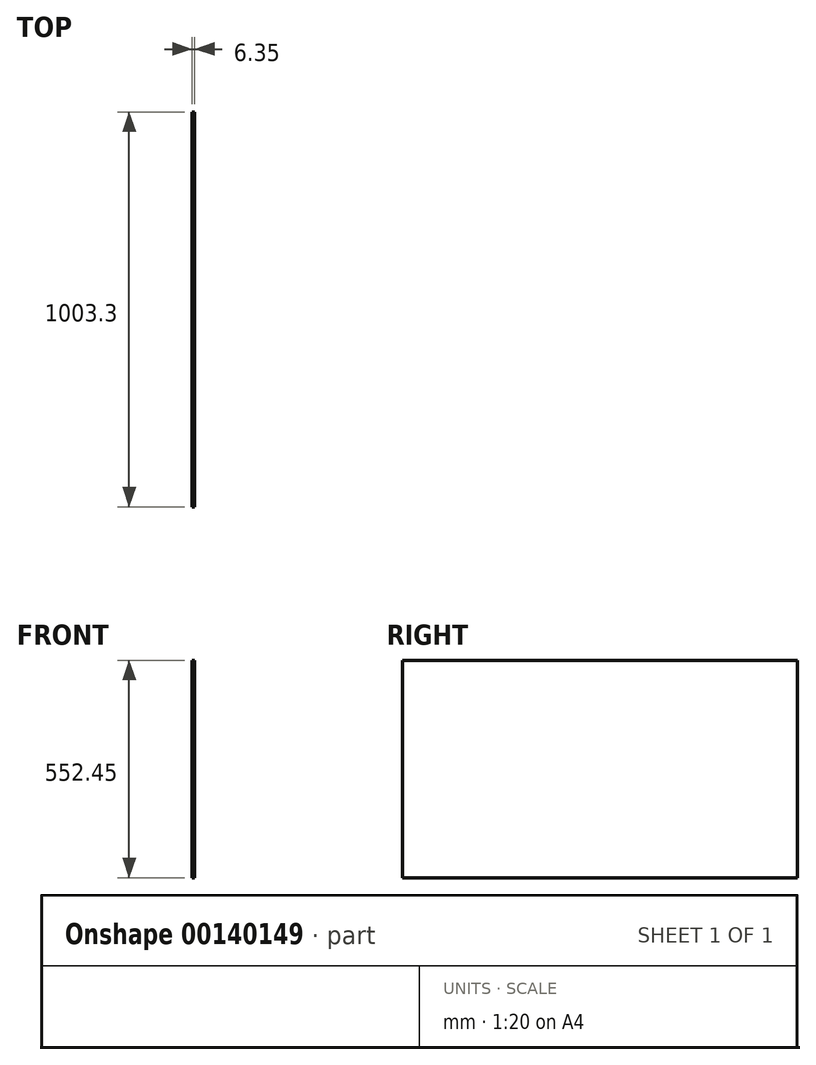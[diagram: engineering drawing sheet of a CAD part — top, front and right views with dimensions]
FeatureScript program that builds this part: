
annotation { "Feature Type Name" : "Feature", "Feature Type Description" : "" }
export const myFeature = defineFeature(function(context is Context, id is Id, definition is map)
    precondition{}
    {
        {
            var Q0;
            Q0=qCreatedBy(makeId("Front.planeOp"),FACE);
            var sketch = newSketch(context, id + "F0", { "sketchPlane" : qUnion([Q0])});
            skLineSegment(sketch, "E0", {"start": v(-200.02, 723.9) * mm, "end": v(-200.03, 171.45) * mm});
            skLineSegment(sketch, "E1", {"start": v(-206.38, 723.9) * mm, "end": v(-206.38, 171.45) * mm});
            skLineSegment(sketch, "E2", {"start": v(-206.38, 171.45) * mm, "end": v(-200.03, 171.45) * mm});
            skLineSegment(sketch, "E3", {"start": v(-206.38, 723.9) * mm, "end": v(-200.02, 723.9) * mm});
            skSolve(sketch);
        }
        {
            var Q0;
            Q0=makeQuery(id+"F0.imprint","IMPRINT",FACE,{"disambiguationData":[TD([[makeQuery(id+"F0.imprint","IMPRINT",EDGE,{"derivedFrom":sQuery(id+"F0.wireOp",EDGE,"E0")}),-1.0]])]});
            extrude(context, id + "F1", {"entities" : qUnion([Q0]), "depth" : 1003.3 * mm});
        }
    });
